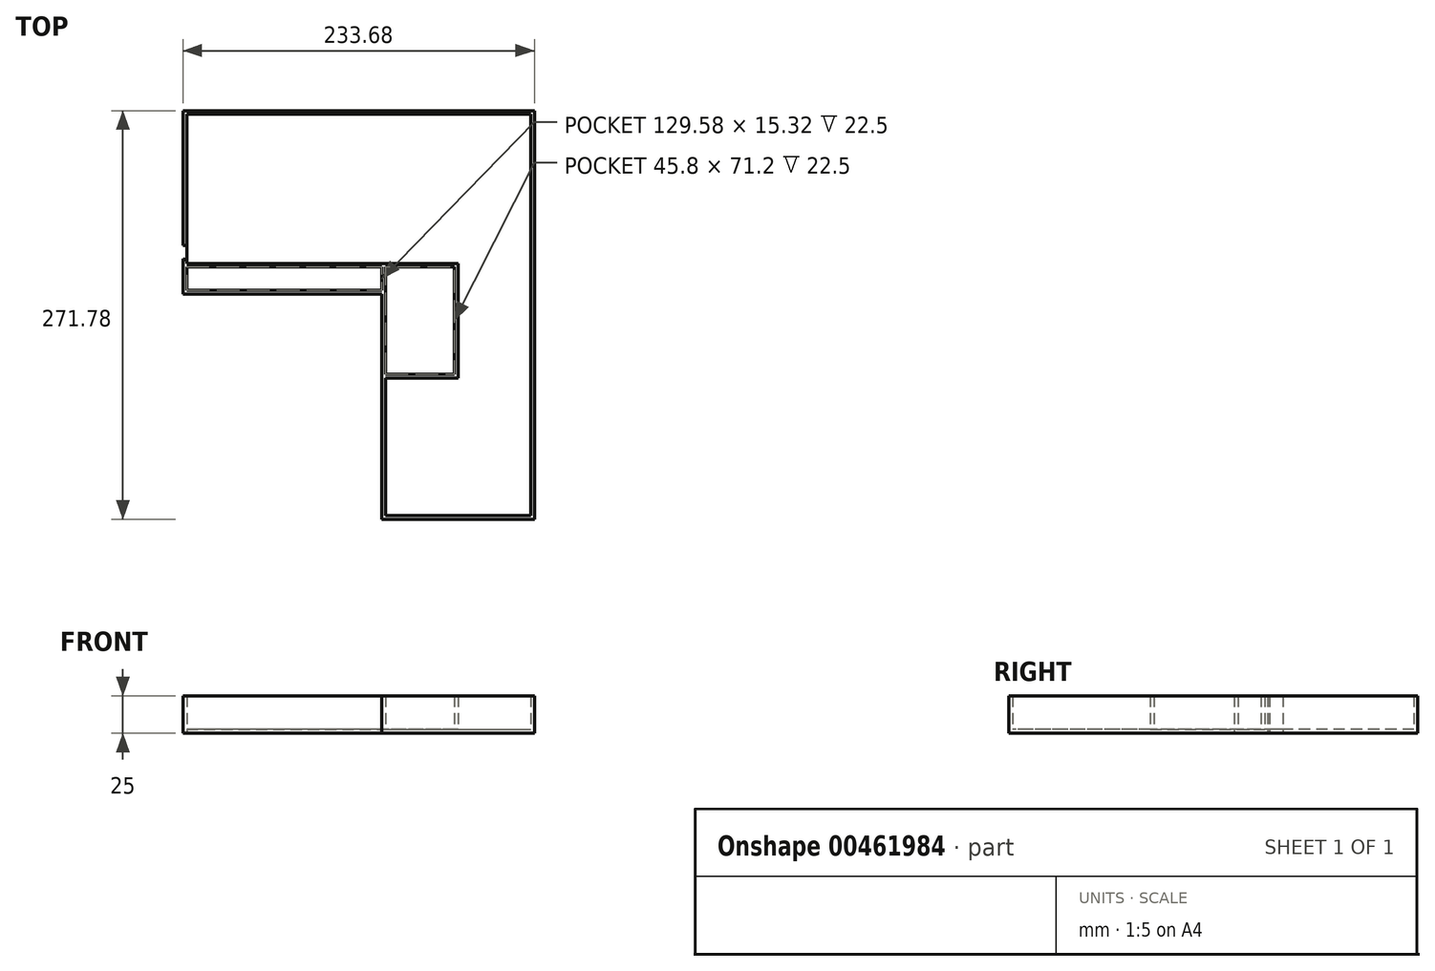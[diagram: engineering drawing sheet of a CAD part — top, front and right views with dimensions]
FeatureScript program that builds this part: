
annotation { "Feature Type Name" : "Feature", "Feature Type Description" : "" }
export const myFeature = defineFeature(function(context is Context, id is Id, definition is map)
    precondition{}
    {
        {
            var Q0;
            Q0=qCreatedBy(makeId("Top.planeOp"),FACE);
            var sketch = newSketch(context, id + "F0", { "sketchPlane" : qUnion([Q0])});
            skLineSegment(sketch, "E0", {"start": v(-361.37, 48.76) * mm, "end": v(-229.29, 48.76) * mm});
            skLineSegment(sketch, "E1", {"start": v(-229.29, 48.76) * mm, "end": v(-229.29, -121.42) * mm});
            skLineSegment(sketch, "E2", {"start": v(-229.29, -121.42) * mm, "end": v(-127.69, -121.42) * mm});
            skLineSegment(sketch, "E3", {"start": v(-229.29, -27.44) * mm, "end": v(-129.45, -27.44) * mm});
            skLineSegment(sketch, "E4", {"start": v(-148, 150.36) * mm, "end": v(-148, -27.44) * mm});
            skLineSegment(sketch, "E5", {"start": v(-361.37, 150.36) * mm, "end": v(-361.37, 74.16) * mm});
            skLineSegment(sketch, "E6", {"start": v(-361.37, 150.36) * mm, "end": v(-272.47, 150.36) * mm});
            skLineSegment(sketch, "E7", {"start": v(-148, 150.36) * mm, "end": v(-236.9, 150.36) * mm});
            skLineSegment(sketch, "E8", {"start": v(-361.37, 48.76) * mm, "end": v(-361.37, 28.44) * mm});
            skLineSegment(sketch, "E9", {"start": v(-361.37, 28.44) * mm, "end": v(-229.29, 28.44) * mm});
            skLineSegment(sketch, "E10", {"start": v(-285.17, 48.76) * mm, "end": v(-285.17, 28.44) * mm});
            skLineSegment(sketch, "E11", {"start": v(-229.29, 48.76) * mm, "end": v(-178.49, 48.76) * mm});
            skLineSegment(sketch, "E12", {"start": v(-178.49, 48.76) * mm, "end": v(-178.49, -27.44) * mm});
            skLineSegment(sketch, "E13", {"start": v(-148, 150.36) * mm, "end": v(-127.69, 150.36) * mm});
            skLineSegment(sketch, "E14", {"start": v(-127.69, 150.36) * mm, "end": v(-127.69, -121.42) * mm});
            skLineSegment(sketch, "E15", {"start": v(-272.47, 150.36) * mm, "end": v(-236.9, 150.36) * mm});
            skLineSegment(sketch, "E16", {"start": v(-361.37, 74.16) * mm, "end": v(-361.37, 48.76) * mm});
            skSolve(sketch);
        }
        {
            var Q0;
            Q0 = qSketchRegion(id + "F0", true);
            var Q1;
            Q1 = qConstructionFilter(qBodyType(qCreatedBy(id + "F0" ,EDGE), BodyType.WIRE), ConstructionObject.NO);
            extrude(context, id + "F1", {"entities" : qUnion([Q0]), "surfaceEntities" : qUnion([Q1]), "depth" : 25 * mm});
        }
        {
            var Q0;
            Q0=makeQuery(id+"F1.opExtrude","CAP_FACE",FACE,{"disambiguationData":[OSD([sQuery(id+"F0.wireOp",EDGE,"E0"),sQuery(id+"F0.wireOp",EDGE,"E1"),sQuery(id+"F0.wireOp",EDGE,"E2"),sQuery(id+"F0.wireOp",EDGE,"E3"),sQuery(id+"F0.wireOp",EDGE,"E4"),sQuery(id+"F0.wireOp",EDGE,"E8"),sQuery(id+"F0.wireOp",EDGE,"E9"),sQuery(id+"F0.wireOp",EDGE,"E11"),sQuery(id+"F0.wireOp",EDGE,"E12"),sQuery(id+"F0.wireOp",EDGE,"E13"),sQuery(id+"F0.wireOp",EDGE,"E14")])],"isStart":false});
            shell(context, id + "F2", {"entities" : qUnion([Q0]), "thickness" : 2.5 * mm});
        }
        {
            var Q0;
            Q0=makeQuery(id+"F2.opShell","OFFSET_FACE",FACE,{"disambiguationData":[OSD([sQuery(id+"F0.wireOp",EDGE,"E1"),sQuery(id+"F0.wireOp",EDGE,"E2"),sQuery(id+"F0.wireOp",EDGE,"E5"),sQuery(id+"F0.wireOp",EDGE,"E6"),sQuery(id+"F0.wireOp",EDGE,"E7"),sQuery(id+"F0.wireOp",EDGE,"E8"),sQuery(id+"F0.wireOp",EDGE,"E9"),sQuery(id+"F0.wireOp",EDGE,"E13"),sQuery(id+"F0.wireOp",EDGE,"E14"),sQuery(id+"F0.wireOp",EDGE,"E15"),sQuery(id+"F0.wireOp",EDGE,"E16")])]});
            var sketch = newSketch(context, id + "F3", { "sketchPlane" : qUnion([Q0])});
            skLineSegment(sketch, "E17", {"start": v(-226.79, 48.76) * mm, "end": v(-361.37, 48.76) * mm});
            skLineSegment(sketch, "E18", {"start": v(-361.37, 48.76) * mm, "end": v(-361.37, 28.44) * mm});
            skLineSegment(sketch, "E19", {"start": v(-226.79, 28.44) * mm, "end": v(-226.79, 48.76) * mm});
            skLineSegment(sketch, "E20", {"start": v(-226.79, 28.44) * mm, "end": v(-361.37, 28.44) * mm});
            skSolve(sketch);
        }
        {
            var Q0;
            Q0 = qSketchRegion(id + "F3", true);
            extrude(context, id + "F4", {"entities" : qUnion([Q0]), "operationType" : NewBodyOperationType.ADD, "depth" : 22.5 * mm});
        }
        {
            var Q0;
            Q0=makeQuery(id+"F4.opExtrude","CAP_FACE",FACE,{"disambiguationData":[OSD([sQuery(id+"F3.wireOp",EDGE,"E17"),sQuery(id+"F3.wireOp",EDGE,"t83Jkana-udiU-vnk9-WF42-tp0BWAvRlzS8"),sQuery(id+"F3.wireOp",EDGE,"Hoemouwr-xIbM-eJzR-CiVC-mtJjTbxUCgjd"),sQuery(id+"F3.wireOp",EDGE,"E18")])],"isStart":false});
            shell(context, id + "F5", {"entities" : qUnion([Q0]), "thickness" : 2.5 * mm});
        }
        {
            var Q0;
            Q0=qCreatedBy(makeId("Top.planeOp"),FACE);
            var sketch = newSketch(context, id + "F6", { "sketchPlane" : qUnion([Q0])});
            skLineSegment(sketch, "E21.bottom", {"start": v(-226.79, 48.76) * mm, "end": v(-178.49, 48.76) * mm});
            skLineSegment(sketch, "E21.top", {"start": v(-226.79, -27.44) * mm, "end": v(-178.49, -27.44) * mm});
            skLineSegment(sketch, "E21.left", {"start": v(-226.79, 48.76) * mm, "end": v(-226.79, -27.44) * mm});
            skLineSegment(sketch, "E21.right", {"start": v(-178.49, 48.76) * mm, "end": v(-178.49, -27.44) * mm});
            skSolve(sketch);
        }
        {
            var Q0;
            Q0 = qSketchRegion(id + "F6", true);
            extrude(context, id + "F7", {"entities" : qUnion([Q0]), "operationType" : NewBodyOperationType.ADD, "depth" : 25 * mm});
        }
        {
            var Q0;
            Q0=makeQuery(id+"F7.boolean.opBoolean","MERGE",FACE,{"derivedFrom":[makeQuery(id+"F4.boolean.opBoolean","MERGE",FACE,{"derivedFrom":[makeQuery(id+"F1.opExtrude","CAP_FACE",FACE,{"disambiguationData":[OSD([sQuery(id+"F0.wireOp",EDGE,"E1"),sQuery(id+"F0.wireOp",EDGE,"E2"),sQuery(id+"F0.wireOp",EDGE,"E5"),sQuery(id+"F0.wireOp",EDGE,"E6"),sQuery(id+"F0.wireOp",EDGE,"E7"),sQuery(id+"F0.wireOp",EDGE,"E8"),sQuery(id+"F0.wireOp",EDGE,"E9"),sQuery(id+"F0.wireOp",EDGE,"E13"),sQuery(id+"F0.wireOp",EDGE,"E14"),sQuery(id+"F0.wireOp",EDGE,"E15"),sQuery(id+"F0.wireOp",EDGE,"E16")])],"isStart":false}),makeQuery(id+"F4.opExtrude","CAP_FACE",FACE,{"disambiguationData":[OSD([sQuery(id+"F3.wireOp",EDGE,"E17"),sQuery(id+"F3.wireOp",EDGE,"E18"),sQuery(id+"F3.wireOp",EDGE,"E19"),sQuery(id+"F3.wireOp",EDGE,"E20")])],"isStart":false})]}),makeQuery(id+"F7.opExtrude","CAP_FACE",FACE,{"disambiguationData":[OSD([sQuery(id+"F6.wireOp",EDGE,"E21.bottom"),sQuery(id+"F6.wireOp",EDGE,"E21.top"),sQuery(id+"F6.wireOp",EDGE,"E21.left"),sQuery(id+"F6.wireOp",EDGE,"E21.right")])],"isStart":false})]});
            shell(context, id + "F8", {"entities" : qUnion([Q0]), "thickness" : 2.5 * mm});
        }
        {
            var Q0;
            Q0=qCreatedBy(makeId("Top.planeOp"),FACE);
            var sketch = newSketch(context, id + "F9", { "sketchPlane" : qUnion([Q0])});
            skLineSegment(sketch, "E22", {"start": v(-361.37, 60.76) * mm, "end": v(-361.37, 51.76) * mm});
            skLineSegment(sketch, "E23", {"start": v(-361.37, 60.76) * mm, "end": v(-358.87, 60.76) * mm});
            skLineSegment(sketch, "E24", {"start": v(-358.87, 60.76) * mm, "end": v(-358.87, 50.76) * mm});
            skLineSegment(sketch, "E25", {"start": v(-358.87, 50.76) * mm, "end": v(-361.37, 51.76) * mm});
            skSolve(sketch);
        }
        {
            var Q0;
            Q0 = qSketchRegion(id + "F9", true);
            extrude(context, id + "F10", {"entities" : qUnion([Q0]), "operationType" : NewBodyOperationType.REMOVE, "depth" : 30 * mm});
        }
    });
